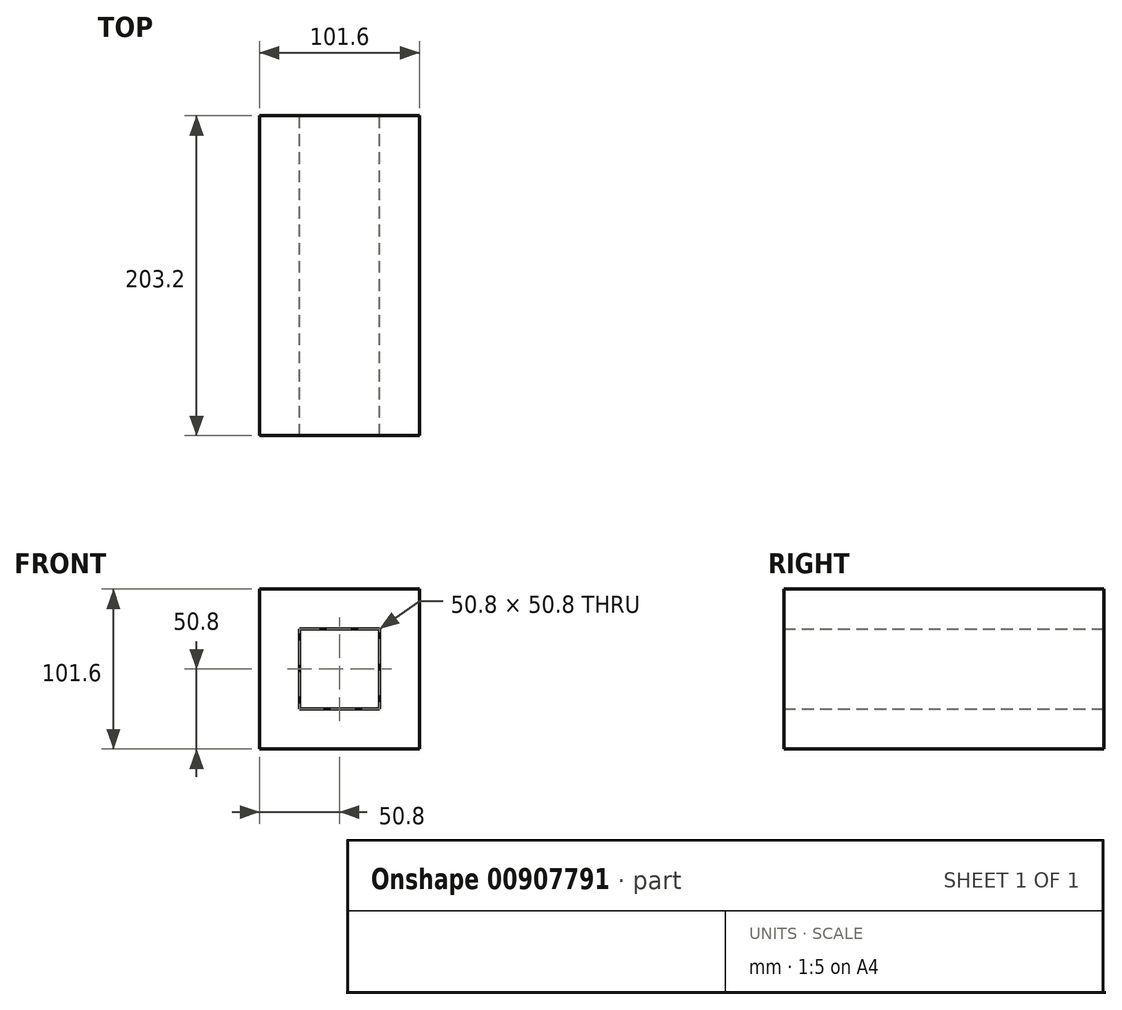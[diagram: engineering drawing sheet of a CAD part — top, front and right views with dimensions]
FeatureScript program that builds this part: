
annotation { "Feature Type Name" : "Feature", "Feature Type Description" : "" }
export const myFeature = defineFeature(function(context is Context, id is Id, definition is map)
    precondition{}
    {
        {
            var Q0;
            Q0=qCreatedBy(makeId("Front.planeOp"),FACE);
            var sketch = newSketch(context, id + "F0", { "sketchPlane" : qUnion([Q0])});
            skLineSegment(sketch, "E0.bottom", {"start": v(-50.8, 50.8) * mm, "end": v(50.8, 50.8) * mm});
            skLineSegment(sketch, "E0.top", {"start": v(-50.8, -50.8) * mm, "end": v(50.8, -50.8) * mm});
            skLineSegment(sketch, "E0.left", {"start": v(-50.8, 50.8) * mm, "end": v(-50.8, -50.8) * mm});
            skLineSegment(sketch, "E0.right", {"start": v(50.8, 50.8) * mm, "end": v(50.8, -50.8) * mm});
            skLineSegment(sketch, "E1.bottom", {"start": v(25.4, 25.4) * mm, "end": v(-25.4, 25.4) * mm});
            skLineSegment(sketch, "E1.top", {"start": v(25.4, -25.4) * mm, "end": v(-25.4, -25.4) * mm});
            skLineSegment(sketch, "E1.left", {"start": v(25.4, 25.4) * mm, "end": v(25.4, -25.4) * mm});
            skLineSegment(sketch, "E1.right", {"start": v(-25.4, 25.4) * mm, "end": v(-25.4, -25.4) * mm});
            skPoint(sketch, "E1.middle", {"position": v(0, 0) * mm});
            skSolve(sketch);
        }
        {
            var Q0;
            Q0 = qSketchRegion(id + "F0", true);
            extrude(context, id + "F1", {"entities" : qUnion([Q0]), "depth" : 203.2 * mm, "offsetDistance" : 25.4 * mm, "symmetric" : true});
        }
    });
